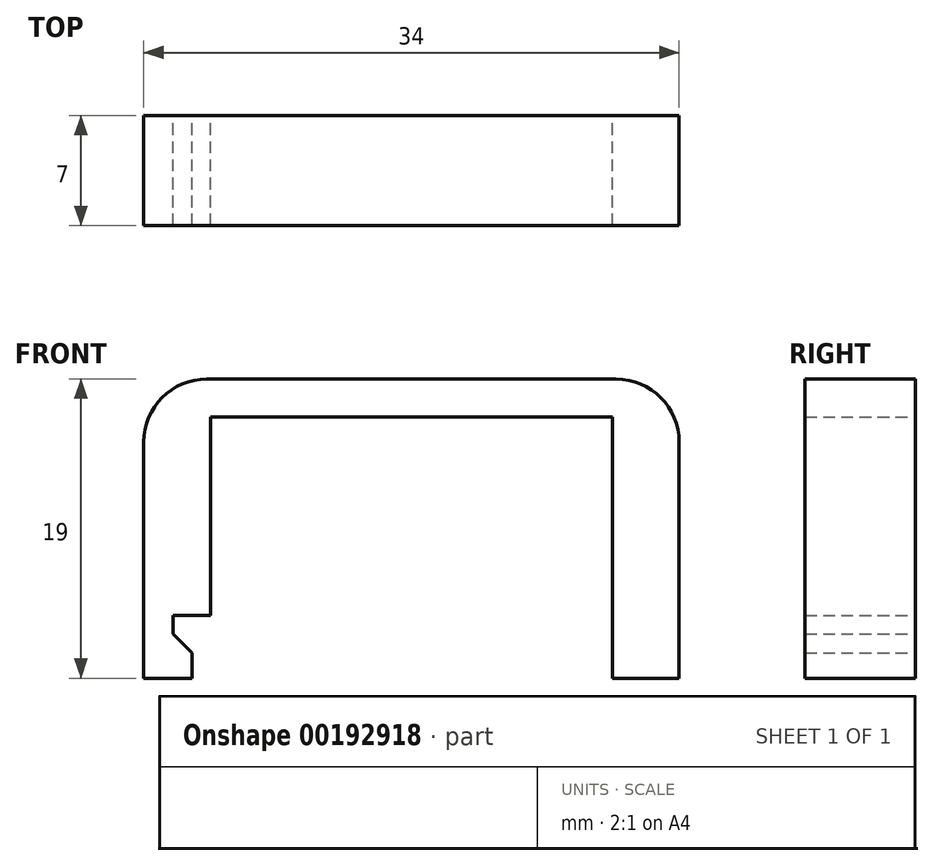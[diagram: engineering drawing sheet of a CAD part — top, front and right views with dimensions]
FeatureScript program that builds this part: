
annotation { "Feature Type Name" : "Feature", "Feature Type Description" : "" }
export const myFeature = defineFeature(function(context is Context, id is Id, definition is map)
    precondition{}
    {
        {
            var Q0;
            Q0=qCreatedBy(makeId("Top.planeOp"),FACE);
            var sketch = newSketch(context, id + "F0", { "sketchPlane" : qUnion([Q0])});
            skLineSegment(sketch, "E0.bottom", {"start": v(17, -3.5) * mm, "end": v(-17, -3.5) * mm});
            skLineSegment(sketch, "E0.top", {"start": v(17, 3.5) * mm, "end": v(-17, 3.5) * mm});
            skLineSegment(sketch, "E0.left", {"start": v(17, -3.5) * mm, "end": v(17, 3.5) * mm});
            skLineSegment(sketch, "E0.right", {"start": v(-17, -3.5) * mm, "end": v(-17, 3.5) * mm});
            skPoint(sketch, "E0.middle", {"position": v(0, 0) * mm});
            skSolve(sketch);
        }
        {
            var Q0;
            Q0 = qSketchRegion(id + "F0", true);
            extrude(context, id + "F1", {"entities" : qUnion([Q0]), "depth" : 2.4 * mm});
        }
        {
            var Q0;
            Q0=makeQuery(id+"F1.opExtrude","SWEPT_FACE",FACE,{"disambiguationData":[OSD([sQuery(id+"F0.wireOp",EDGE,"E0.top")])]});
            var sketch = newSketch(context, id + "F2", { "sketchPlane" : qUnion([Q0])});
            skLineSegment(sketch, "E1.bottom", {"start": v(-12.75, 23.45) * mm, "end": v(12.75, 23.45) * mm});
            skLineSegment(sketch, "E1.top", {"start": v(-12.75, -21.71) * mm, "end": v(12.75, -21.71) * mm});
            skLineSegment(sketch, "E1.left", {"start": v(-12.75, 23.45) * mm, "end": v(-12.75, -21.71) * mm});
            skLineSegment(sketch, "E1.right", {"start": v(12.75, 23.45) * mm, "end": v(12.75, -21.71) * mm});
            skPoint(sketch, "E1.middle", {"position": v(0, 0.87) * mm});
            skLineSegment(sketch, "E2.bottom", {"start": v(17, 2.4) * mm, "end": v(12.75, 2.4) * mm});
            skLineSegment(sketch, "E2.top", {"start": v(17, -16.6) * mm, "end": v(12.75, -16.6) * mm});
            skLineSegment(sketch, "E2.left", {"start": v(17, 2.4) * mm, "end": v(17, -16.6) * mm});
            skLineSegment(sketch, "E2.right", {"start": v(12.75, 2.4) * mm, "end": v(12.75, -16.6) * mm});
            skLineSegment(sketch, "E3.bottom", {"start": v(-17, 2.4) * mm, "end": v(-12.75, 2.4) * mm});
            skLineSegment(sketch, "E3.top", {"start": v(-17, -16.6) * mm, "end": v(-12.75, -16.6) * mm});
            skLineSegment(sketch, "E3.left", {"start": v(-17, 2.4) * mm, "end": v(-17, -16.6) * mm});
            skLineSegment(sketch, "E3.right", {"start": v(-12.75, 2.4) * mm, "end": v(-12.75, -16.6) * mm});
            skSolve(sketch);
        }
        {
            var Q0;
            {var subQ0=sQuery(id+"F2.wireOp",EDGE,"E2.top");Q0=makeQuery(id+"F2.imprint","IMPRINT",FACE,{"disambiguationData":[TD([[makeQuery(id+"F2.imprint","IMPRINT",EDGE,{"derivedFrom":subQ0}),-1.0]])]});}
            var Q1;
            {var subQ0=sQuery(id+"F2.wireOp",EDGE,"E3.top");Q1=makeQuery(id+"F2.imprint","IMPRINT",FACE,{"disambiguationData":[TD([[makeQuery(id+"F2.imprint","IMPRINT",EDGE,{"derivedFrom":subQ0}),1.0]])]});}
            extrude(context, id + "F3", {"entities" : qUnion([Q0, Q1]), "operationType" : NewBodyOperationType.ADD, "oppositeDirection" : true, "depth" : 7 * mm});
        }
        {
            var Q0;
            {var subQ0=sQuery(id+"F0.wireOp",EDGE,"E0.top");Q0=makeQuery(id+"F3.boolean.opBoolean","MERGE",FACE,{"derivedFrom":[makeQuery(id+"F1.opExtrude","SWEPT_FACE",FACE,{"disambiguationData":[OSD([subQ0])]}),makeQuery(id+"F3.opExtrude","CAP_FACE",FACE,{"disambiguationData":[OSD([subQ0,sQuery(id+"F2.wireOp",EDGE,"E2.top"),sQuery(id+"F2.wireOp",EDGE,"E2.left"),sQuery(id+"F2.wireOp",EDGE,"E2.right")])],"isStart":true}),makeQuery(id+"F3.opExtrude","CAP_FACE",FACE,{"disambiguationData":[OSD([subQ0,sQuery(id+"F2.wireOp",EDGE,"E3.top"),sQuery(id+"F2.wireOp",EDGE,"E3.left"),sQuery(id+"F2.wireOp",EDGE,"E3.right")])],"isStart":true})]});}
            var sketch = newSketch(context, id + "F4", { "sketchPlane" : qUnion([Q0])});
            skLineSegment(sketch, "E4", {"start": v(12.75, -16.6) * mm, "end": v(12.75, -12.6) * mm});
            skLineSegment(sketch, "E5", {"start": v(12.75, -12.6) * mm, "end": v(15.15, -12.6) * mm});
            skLineSegment(sketch, "E6", {"start": v(15.15, -12.6) * mm, "end": v(15.15, -13.8) * mm});
            skLineSegment(sketch, "E7", {"start": v(15.15, -13.8) * mm, "end": v(13.95, -15) * mm});
            skLineSegment(sketch, "E8", {"start": v(13.95, -15) * mm, "end": v(13.95, -16.6) * mm});
            skLineSegment(sketch, "E9", {"start": v(13.95, -16.6) * mm, "end": v(12.75, -16.6) * mm});
            skSolve(sketch);
        }
        {
            var Q0;
            Q0 = qSketchRegion(id + "F4", true);
            extrude(context, id + "F5", {"entities" : qUnion([Q0]), "operationType" : NewBodyOperationType.REMOVE, "oppositeDirection" : true, "depth" : 10 * mm});
        }
        {
            var Q0;
            Q0=makeQuery(id+"F1.opExtrude","CAP_EDGE",EDGE,{"disambiguationData":[OSD([sQuery(id+"F0.wireOp",EDGE,"E0.left")])],"isStart":false});
            var Q1;
            Q1=makeQuery(id+"F1.opExtrude","CAP_EDGE",EDGE,{"disambiguationData":[OSD([sQuery(id+"F0.wireOp",EDGE,"E0.right")])],"isStart":false});
            fillet(context, id + "F6", {"entities" : qUnion([Q0, Q1]), "radius" : 4 * mm, "tangentPropagation" : true, "allowEdgeOverflow" : false});
        }
    });
